# Revit family: Квайт_Eng
name_source: partatom
category: Mechanical Equipment
units: mm (PartAtom-declared; Revit-internal decimal feet)

## family parameters
Always vertical = Yes
Classification = None
Cut with Voids When Loaded = No
Part Type = Normal
Room Calculation Point = No
Round Connector Dimension = Use Diameter
Shared = No
Work Plane-Based = No

## types (3) — shared parameters
00_20_Manufacturer = Vents
00_20_Name = Axial fan
Amperage = 0 A
Casing Material = Plastic, opaque, white
Frequency = 50 Hz
Load Classification = HVAC
Maintenance zone material = <By Category>
Manufacturer = Vents
Number of Fase = 1
URL = https://ventilation-system.com
Voltage = 230 V
zero-valued in all types: Default Elevation

## per-type parameters (varying)
| type | B | D | Diameter | Dy | H | Height | L | L1 | L2 | Length | Maximum Air Flow | Power | Sound pressure level at 3 m distance | Weight | Width |
| Quiet 100 | 158 mm | 100 mm  [stored 0.328084 ft] | 100 mm  [stored 0.328084 ft] | 96 mm  [stored 0.314961 ft] | 158 mm | 158 mm | 81 mm  [stored 0.265748 ft] | 26 mm | 55 mm  [stored 0.180446 ft] | 81 mm  [stored 0.265748 ft] | 97.0 m³/h | 8 W | 25 dBA | 0.55 kg | 158 mm |
| Quiet 125 | 182 mm  [stored 0.597113 ft] | 125 mm  [stored 0.410105 ft] | 125 mm  [stored 0.410105 ft] | 121 mm  [stored 0.396982 ft] | 182 mm  [stored 0.597113 ft] | 182 mm  [stored 0.597113 ft] | 91 mm  [stored 0.298556 ft] | 27 mm  [stored 0.0885827 ft] | 64 mm  [stored 0.209974 ft] | 91 mm  [stored 0.298556 ft] | 185.0 m³/h | 17 W | 32 dBA | 0.78 kg | 182 mm  [stored 0.597113 ft] |
| Quiet 150 | 214 mm  [stored 0.7021 ft] | 150 mm | 150 mm | 146 mm  [stored 0.479003 ft] | 214 mm  [stored 0.7021 ft] | 214 mm  [stored 0.7021 ft] | 111 mm | 32 mm  [stored 0.104987 ft] | 79 mm  [stored 0.259186 ft] | 111 mm | 315.0 m³/h | 19 W | 33 dBA | 1.33 kg | 214 mm  [stored 0.7021 ft] |

note: column(s) folded — value = type name in every type: 00_20_Type

note: [stored X ft] marks values corroborated as IEEE doubles in the binary element streams (Revit-internal decimal feet)
